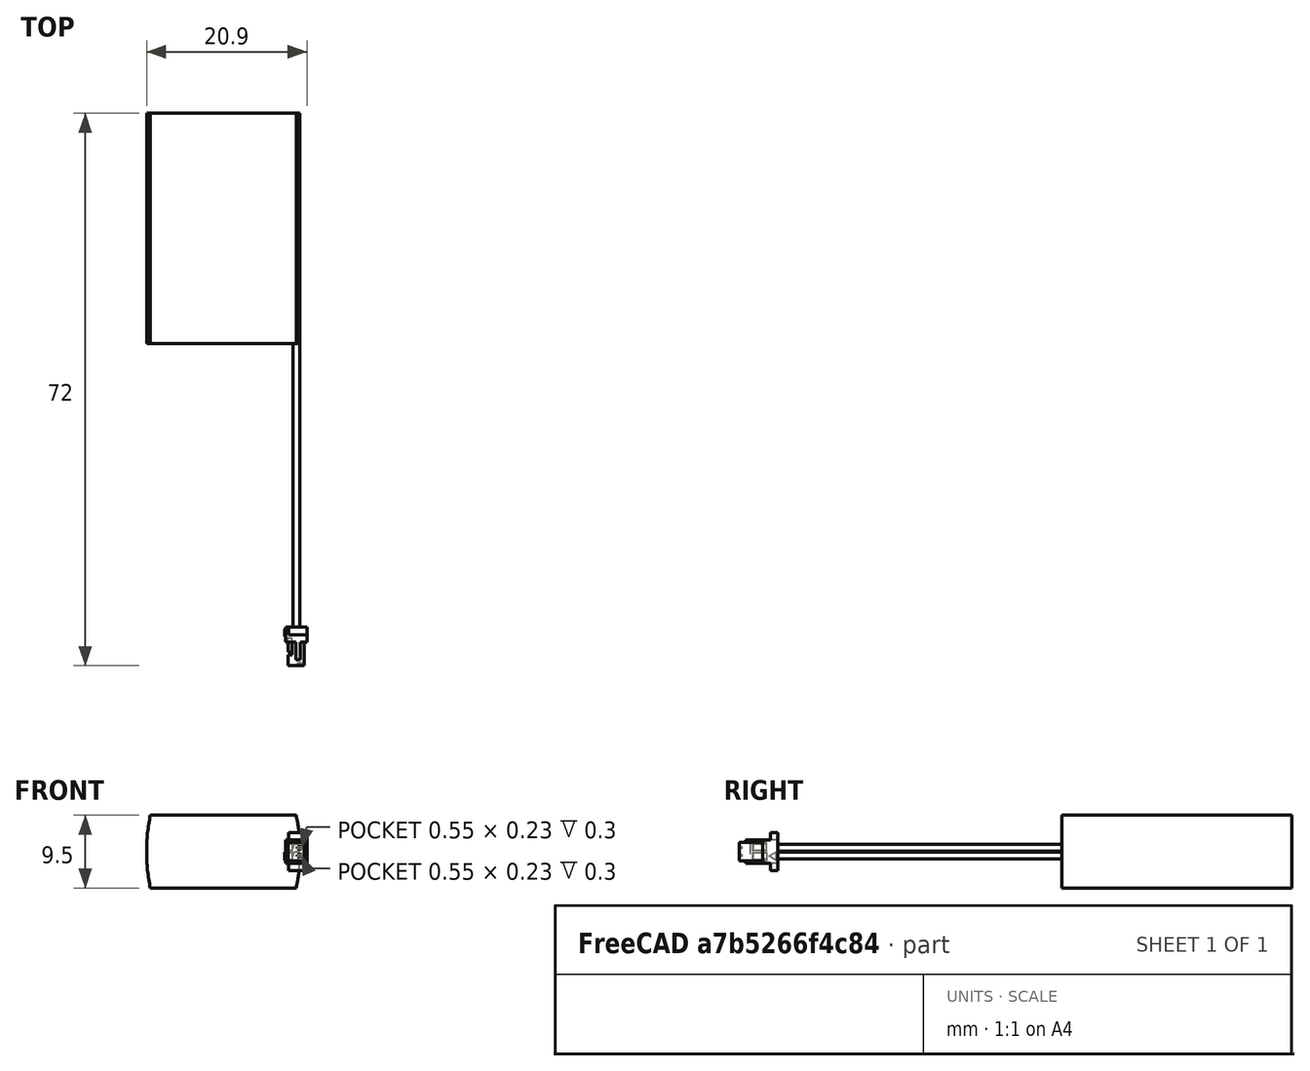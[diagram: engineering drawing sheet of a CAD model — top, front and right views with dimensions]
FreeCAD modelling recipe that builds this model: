
FCSTD DOCUMENT  (FreeCAD 2021.519R24301 +3652 (Git))
Label: ASR00035_500mAh
License: Other
objects: TechDraw::DrawViewDimension×4, Sketcher::SketchObject×3, PartDesign::Pad×3, TechDraw::DrawViewPart×2, TechDraw::DrawViewAnnotation×2, PartDesign::Pocket×1, PartDesign::Mirrored×1, PartDesign::Body×1, Part::Feature×1, Part::MultiFuse×1, TechDraw::DrawSVGTemplate×1, TechDraw::DrawPage×1, Mesh::Feature×1
note: 21 computed .brp shape members not serialized (recipe doc carries the construction recipe); baked Part::Feature solids carry a one-line shape summary decoded from their .brp

FEATURE [Sketcher::SketchObject] Sketch
  FullyConstrained = true
  MapMode = 5
  Support = -> [XY_Plane]
  sketch-geometry (4):
    g0: LineSegment StartX=-10 StartY=15 StartZ=0 EndX=10 EndY=15 EndZ=0
    g1: LineSegment StartX=10 StartY=15 StartZ=0 EndX=10 EndY=-15 EndZ=0
    g2: LineSegment StartX=10 StartY=-15 StartZ=0 EndX=-10 EndY=-15 EndZ=0
    g3: LineSegment StartX=-10 StartY=-15 StartZ=0 EndX=-10 EndY=15 EndZ=0
  constraints (10):
    c: Coincident(g0,g1)
    c: Coincident(g1,g2)
    c: Coincident(g2,g3)
    c: Coincident(g3,g0)
    c: Horizontal(g2)
    c: Vertical(g1)
    c: Symmetric(g0,g2,g-1)
    c: Symmetric(g0,g0,g-2)
    c: DistanceX(g0,g0) = 20
    c: DistanceY(g3,g3) = 30
FEATURE [PartDesign::Pad] Pad
  ClaimChildren = false
  Direction = (1,1,1)
  Fit = 0
  FitJoin = 0
  InnerFit = 0
  InnerFitJoin = 0
  InnerTaperAngle = 0
  InnerTaperAngleRev = 0
  Length = 9.5
  Length2 = 100
  Midplane = true
  NewSolid = false
  Profile = -> Sketch
  Suppress = false
  Type = 0
FEATURE [Sketcher::SketchObject] Sketch001
  ExternalGeometry = -> [Pad]
  FullyConstrained = true
  MapMode = 5
  Placement = pos=(0,15,0) rot=(0,0.707107,0.707107;3.14159rad)
  Support = -> [Pad]
  sketch-geometry (5):
    g0: ArcOfCircle CenterX=12.8125 CenterY=2.3e-15 CenterZ=0 NormalX=0 NormalY=0 NormalZ=1 AngleXU=0 Radius=22.8125 StartAngle=2.93184 EndAngle=3.35135
    g1: LineSegment [constr] StartX=-9.5 StartY=-4.75 StartZ=0 EndX=-9.5 EndY=4.75 EndZ=0
    g2: LineSegment StartX=-9.5 StartY=-4.75 StartZ=0 EndX=-11 EndY=-4.75 EndZ=0
    g3: LineSegment StartX=-9.5 StartY=4.75 StartZ=0 EndX=-11 EndY=4.75 EndZ=0
    g4: LineSegment StartX=-11 StartY=4.75 StartZ=0 EndX=-11 EndY=-4.75 EndZ=0
  constraints (15):
    c: PointOnObject(g0,g-5)
    c: PointOnObject(g0,g-4)
    c: Tangent(g0,g-3)
    c: Coincident(g1,g0)
    c: Coincident(g1,g0)
    c: Vertical(g1)
    c: Coincident(g2,g0)
    c: Horizontal(g2)
    c: Coincident(g3,g0)
    c: Horizontal(g3)
    c: Coincident(g4,g3)
    c: Coincident(g4,g2)
    c: Vertical(g4)
    c: DistanceX(g3,g-4) = 1
    c: DistanceX(g-4,g0) = 0.5
FEATURE [PartDesign::Pocket] Pocket
  BaseFeature = -> Pad
  ClaimChildren = false
  Fit = 0
  FitJoin = 0
  InnerFit = 0
  InnerFitJoin = 0
  InnerTaperAngle = 0
  InnerTaperAngleRev = 0
  Length = 5
  Length2 = 100
  NewSolid = false
  Profile = -> Sketch001
  Suppress = false
  Type = 1
FEATURE [PartDesign::Mirrored] Mirrored
  BaseFeature = -> Pocket
  CopyShape = true
  MirrorPlane = -> Sketch001 [V_Axis]
  NewSolid = false
  OriginalSubs = -> [Pocket]
  Originals = -> [Pocket]
  ParallelTransform = true
  SubTransform = true
  Suppress = false
FEATURE [PartDesign::Pad] Pad001
  BaseFeature = -> Mirrored
  ClaimChildren = false
  Direction = (1,1,1)
  Fit = 0
  FitJoin = 0
  InnerFit = 0
  InnerFitJoin = 0
  InnerTaperAngle = 0
  InnerTaperAngleRev = 0
  Length = 7.85
  Length2 = 100
  NewSolid = false
  Profile = -> Mirrored [Face8]
  Reversed = true
  Suppress = false
  Type = 0
FEATURE [Sketcher::SketchObject] Sketch002
  ExternalGeometry = -> [Pad001]
  FullyConstrained = true
  MapMode = 5
  Placement = pos=(0,-15,0) rot=(1,0,0;1.5708rad)
  Support = -> [Pad001]
  sketch-geometry (7):
    g0: Circle CenterX=9.5 CenterY=-0.5 CenterZ=0 NormalX=0 NormalY=0 NormalZ=1 AngleXU=0 Radius=0.45
    g1: Circle CenterX=9.5 CenterY=0.5 CenterZ=0 NormalX=0 NormalY=0 NormalZ=1 AngleXU=0 Radius=0.45
    g2: LineSegment [constr] StartX=9.5 StartY=0.5 StartZ=0 EndX=9.5 EndY=-0.5 EndZ=0
    g3: GeomPoint [constr] X=9.5 Y=-0.95 Z=0
    g4: GeomPoint [constr] X=9.5 Y=0.95 Z=0
    g5: LineSegment [constr] StartX=9.05 StartY=-0.5 StartZ=0 EndX=9.95 EndY=-0.5 EndZ=0
    g6: GeomPoint [constr] X=9.5 Y=0.05 Z=0
  constraints (16):
    c: Coincident(g2,g1)
    c: Coincident(g2,g0)
    c: Equal(g0,g1)
    c: Diameter(g0) = 0.9
    c: Symmetric(g0,g1,g-1)
    c: PointOnObject(g3,g2)
    c: PointOnObject(g4,g1)
    c: Symmetric(g3,g4,g-1)
    c: PointOnObject(g5,g0)
    c: PointOnObject(g5,g0)
    c: Horizontal(g5)
    c: PointOnObject(g0,g5)
    c: PointOnObject(g6,g1)
    c: PointOnObject(g6,g2)
    c: DistanceY(g-3,g6) = 0.05
    c: DistanceX(g5,g-3) = 0.05
FEATURE [PartDesign::Pad] Pad002
  BaseFeature = -> Pad001
  ClaimChildren = false
  Direction = (1,1,1)
  Fit = 0
  FitJoin = 0
  InnerFit = 0
  InnerFitJoin = 0
  InnerTaperAngle = 0
  InnerTaperAngleRev = 0
  Length = 37
  Length2 = 100
  NewSolid = false
  Profile = -> Sketch002
  Suppress = false
  Type = 0
FEATURE [PartDesign::Body] Body
  AutoGroupSolids = false
  ExportMode = 0
  Group = -> [Sketch,Pad,Sketch001,Pocket,Mirrored,Pad001,Sketch002,Pad002]
  Origin = -> Origin
  Tip = -> Pad002
  _ExportChildren = -> [Pad,Pocket,Mirrored,Pad001,Pad002]
  _GroupVersion = 1
FEATURE [Part::Feature] Solid  label="Body007"
  Placement = pos=(8.21545,-54,7.1e-15) rot=(0,0,1;0rad)
  shape: bbox 2.9 x 5 x 4.94 mm, 60 faces (baked)
FEATURE [Part::MultiFuse] Fusion
  Shapes = -> [Body,Solid]
FEATURE [TechDraw::DrawSVGTemplate] Template
  Height = 210
  Orientation = 1
  Width = 297
FEATURE [TechDraw::DrawViewPart] View
  CoarseView = false
  Direction = (0,0,1)
  Focus = 100
  HardHidden = false
  IsoCount = 0
  IsoHidden = false
  IsoVisible = false
  LockPosition = false
  Perspective = false
  Rotation = 180
  Scale = 1.52
  ScaleType = 0
  SeamHidden = false
  SeamVisible = true
  SmoothHidden = false
  SmoothVisible = true
  Source = -> [Fusion]
  X = 178.5
  XDirection = (1,0,0)
  Y = 105
FEATURE [TechDraw::DrawViewPart] View001
  CoarseView = false
  Direction = (-1,0,0)
  Focus = 100
  HardHidden = false
  IsoCount = 0
  IsoHidden = false
  IsoVisible = false
  LockPosition = false
  Perspective = false
  Rotation = 90
  Scale = 1.52
  ScaleType = 0
  SeamHidden = false
  SeamVisible = true
  SmoothHidden = false
  SmoothVisible = true
  Source = -> [Fusion]
  X = 118.5
  XDirection = (0,-1,0)
  Y = 105
FEATURE [TechDraw::DrawViewAnnotation] Annotation
  Font = MS Shell Dlg 2
  LineSpace = 80
  LockPosition = false
  MaxWidth = -1
  Rotation = 0
  ScaleType = 0
  Text = SIDE VIEW
  TextSize = 6
  TextStyle = 0
  X = 118.5
  Y = 162
FEATURE [TechDraw::DrawViewAnnotation] Annotation001
  Font = MS Shell Dlg 2
  LineSpace = 80
  LockPosition = false
  MaxWidth = -1
  Rotation = 0
  ScaleType = 0
  Text = TOP VIEW
  TextSize = 6
  TextStyle = 0
  X = 178.5
  Y = 162
FEATURE [TechDraw::DrawViewDimension] Dimension
  Arbitrary = false
  ArbitraryTolerances = false
  EqualTolerance = true
  FormatSpec = %.1f
  FormatSpecOverTolerance = %+.1f
  FormatSpecUnderTolerance = %+.1f
  Inverted = false
  LockPosition = false
  MeasureType = 1
  OverTolerance = 0.5
  References2D = -> [View001]
  Rotation = 0
  ScaleType = 0
  TheoreticalExact = false
  Type = 1
  UnderTolerance = -0.5
  X = -35
  Y = -59
FEATURE [TechDraw::DrawViewDimension] Dimension001
  Arbitrary = false
  ArbitraryTolerances = false
  EqualTolerance = true
  FormatSpec = %.1f
  FormatSpecOverTolerance = %+.1f
  FormatSpecUnderTolerance = %+.1f
  Inverted = false
  LockPosition = false
  MeasureType = 1
  OverTolerance = 2
  References2D = -> [View]
  Rotation = 0
  ScaleType = 0
  TheoreticalExact = false
  Type = 1
  UnderTolerance = -2
  X = 33.684
  Y = -59
FEATURE [TechDraw::DrawViewDimension] Dimension002
  Arbitrary = false
  ArbitraryTolerances = false
  EqualTolerance = true
  FormatSpec = %.1f
  FormatSpecOverTolerance = %+.1f
  FormatSpecUnderTolerance = %+.1f
  Inverted = false
  LockPosition = false
  MeasureType = 1
  OverTolerance = 3
  References2D = -> [View]
  Rotation = 0
  ScaleType = 0
  TheoreticalExact = false
  Type = 2
  UnderTolerance = -3
  X = -32
  Y = -30.3
FEATURE [TechDraw::DrawViewDimension] Dimension003
  Arbitrary = false
  ArbitraryTolerances = false
  EqualTolerance = true
  FormatSpec = %.1f
  FormatSpecOverTolerance = %+.1f
  FormatSpecUnderTolerance = %+.1f
  Inverted = false
  LockPosition = false
  MeasureType = 1
  OverTolerance = 5
  References2D = -> [View]
  Rotation = 0
  ScaleType = 0
  TheoreticalExact = false
  Type = 2
  UnderTolerance = -5
  X = -32
  Y = 20.5
FEATURE [TechDraw::DrawPage] Page
  KeepUpdated = true
  NextBalloonIndex = 1
  ProjectionType = 0
  Template = -> Template
  Views = -> [View,View001,Annotation,Annotation001,Dimension,Dimension001,Dimension002,Dimension003]
FEATURE [Mesh::Feature] Mesh  label="Fusion (Meshed)"
